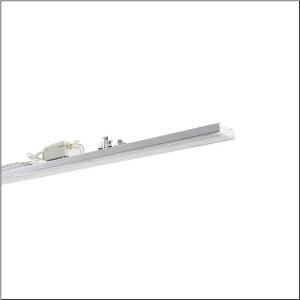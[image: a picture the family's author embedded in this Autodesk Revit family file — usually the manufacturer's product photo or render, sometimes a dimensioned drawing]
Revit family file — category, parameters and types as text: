
# Revit family: licross_21_recessed_ho_52te11dn4e5s
name_source: partatom
category: Lighting Fixtures
units: mm (PartAtom-declared; Revit-internal decimal feet)

## family parameters
Cut with Voids When Loaded = No
Host = Face
Light Source = No
Part Type = Normal
Room Calculation Point = No
Round Connector Dimension = Use Diameter
Shared = No

## types (1)
- --- (1 x LED, 14970 lm, 84.6 W, 4000K)
    Apparent Load = 85 VA
    CIE Flux Codes = 87 95 99 100 100
    Color Rendering = 80
    Color Temperature = 4000K
    Default Elevation = 1800 mm
    Description = Licross 21 Recessed HO, luminaire insert, of sheet steel, galvanised, coil coated, white, length: 1.500mm, width: 66mm, height: 67mm, LED rated luminous flux: 14.970lm, light colour: 840, SDCM (Standard Deviation of Colour Matching)MacAdam ≤ 3 SDCM (initial), control gear: DALI 2, with plug, 5-pole, with phase selection, mains connection: 220..240V, AC, 50/60Hz, rated input power: 85W, internal wiring halogen-free, primary light control with lens, of plastic, primary optical cover: cover, of PMMA, light emission: direct distribution, primary light characteristic: symmetric, protection rating (complete): IP54, insulation class (complete): insulation class I (protective earthing), certification: CE, ENEC, VDE, UKCA, protection symbol: D if used in an environment with non-conductive dust loads with corresponding accessories, impact resistance: IK06, permissible ambient temperature for indoor applications: -25..+30°C, corresponds to IFS (International Featured Standards) requirements for safety and quality in the food industry, reducing of maximum allowable ambient temperature of 5°C with ceiling mounting, LABS conformity tested according to VDMA 24364:2018-05, The light source and the operating device comply with the requirements of the Ecodesign Regulation (EU) 2019/2020 and are replaceable in accordance with this regulation, packaging unit: 1 piece
    Height = 58 mm
    Lamp = 1 x LED
    Lamp Light Flux = 14970 lm
    Lamp Power = 84.6 W
    Lamp count = 1
    Length = 1500 mm
    Luminous efficacy = 177 lm/W
    Manufacturer = Siteco
    ModVariant = No
    Model = 52TE11DN4E5S
    Mounting Place = Ceiling
    Mounting Type = Pendant
    Number of Poles = 1
    OnlyDefault = Yes
    Power Factor = 1
    Product Name = Licross 21 Recessed HO
    Product group = luminaire insert | ceiling pendant
    ProductGroupID = 901
    Protection Class = Protection class I
    Protection Degree = IP 54
    RLX_Detail_Level = 1
    RLX_Emergency_Light_Flux = 0 lm
    RLX_Emergency_Type = 0
    RLX_Emergency_Type_DB = No
    RlxData = <blob elided: 24917 chars, md5=0f160b76>
    Socket = socket
    Standby Power = 0 W
    System Light Flux = 14970 lm
    System Power = 85 W
    Type Comments = factory setting: luminous flux: 100 % | dim-lin: 254 | 484 mA
    Type Image = l_1296930.jpg
    URL = http://relux.com
    VarID = @adj_128893
    Voltage = 0 V
    Weight = 0.00 kg
    Width = 66 mm

## geometry (parser evidence)
native form markers: Blend x4, Sweep x11
no freeform markers — native parametric forms only
